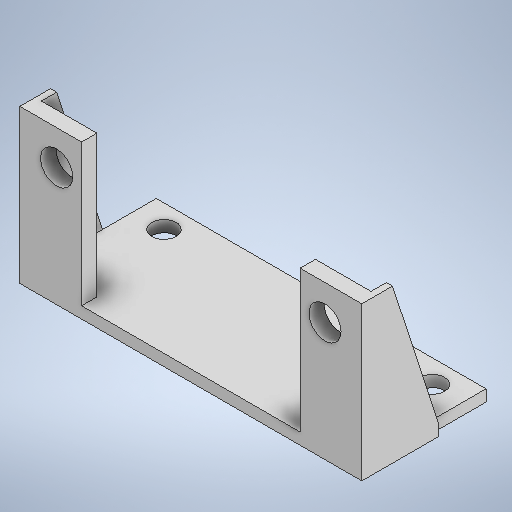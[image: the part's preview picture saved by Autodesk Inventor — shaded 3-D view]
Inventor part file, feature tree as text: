
AUTODESK INVENTOR PART (.ipt)
format: ipt  version: 2025.3 (Build 293356000, 356)  size: 273,408 bytes
history: native  units: mm
features: sketch x3, extrude x3, other x1, hole x1, mirror x1
ambient origin geometry x8: Origin, YZ Plane, XZ Plane, XY Plane, X Axis, Y Axis, Z Axis, Center Point
bodies: Body1 (feature_tree)
feature tree (9):
  other  "ソリッド1"
  sketch  "スケッチ1"
  extrude  "前"  Depth=28.0mm
  extrude  "底"  Depth=1.5mm
  hole  "穴2"  [1 undecoded]
  extrude  "押し出し5"  Depth=4.2mm
  mirror  "ミラー3"
  sketch  "スケッチ5"
  sketch  "スケッチ6"
note: 1 required parameter value undecoded (feature->parameter linkage not recoverable at this tier; creation-order binding heuristic only, values carry confidence <= 0.55)
